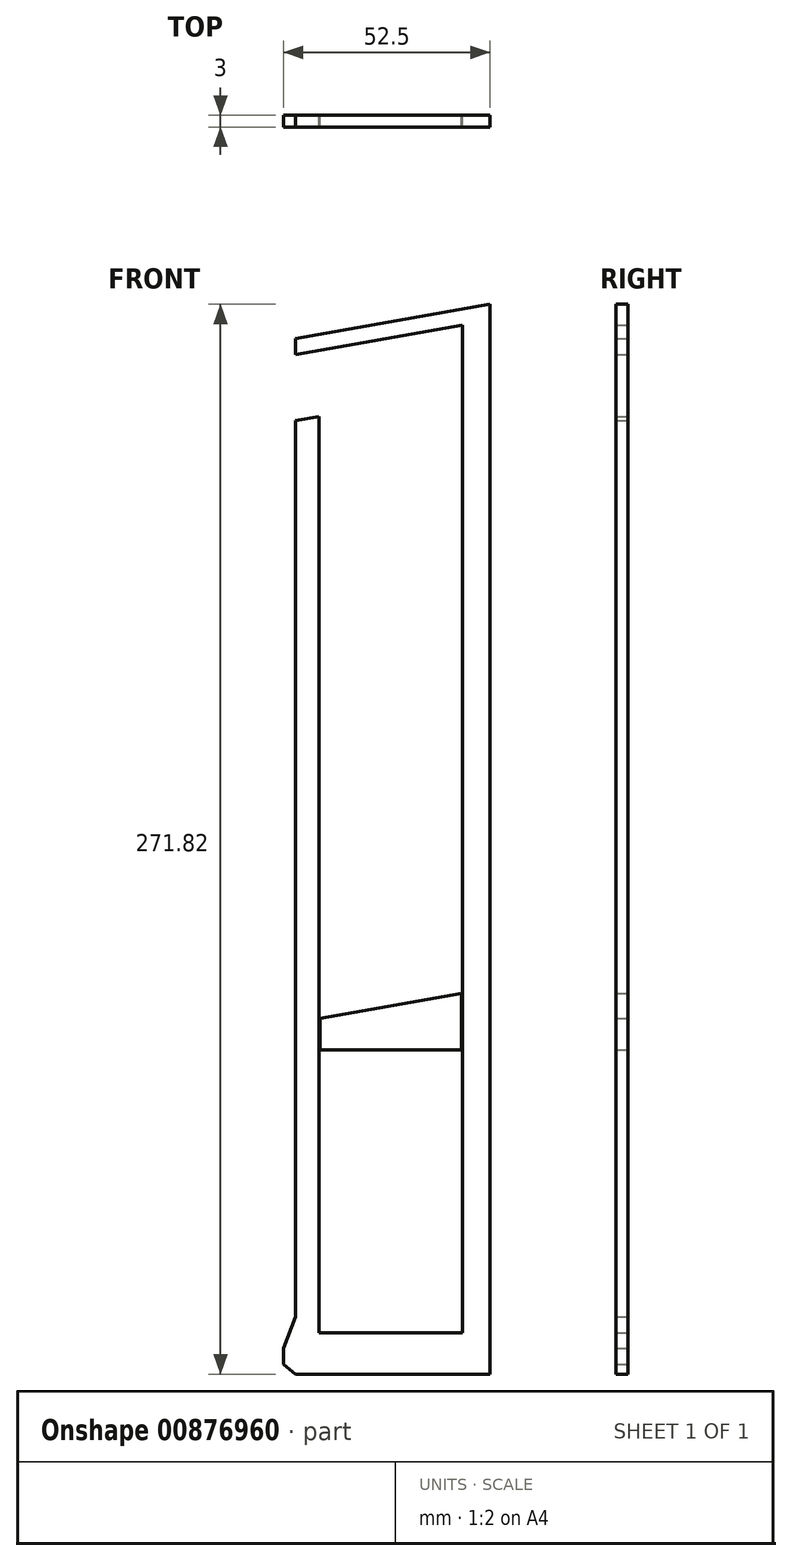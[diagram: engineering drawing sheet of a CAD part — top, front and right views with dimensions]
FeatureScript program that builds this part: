
annotation { "Feature Type Name" : "Feature", "Feature Type Description" : "" }
export const myFeature = defineFeature(function(context is Context, id is Id, definition is map)
    precondition{}
    {
        {
            var Q0;
            Q0=qCreatedBy(makeId("Front.planeOp"),FACE);
            var sketch = newSketch(context, id + "F0", { "sketchPlane" : qUnion([Q0])});
            skLineSegment(sketch, "E0", {"start": v(0, -251) * mm, "end": v(-49.5, -251) * mm});
            skPoint(sketch, "E1", {"position": v(-43.44, -7.66) * mm});
            skPoint(sketch, "E2", {"position": v(-7, -1.23) * mm});
            skLineSegment(sketch, "E3", {"start": v(-49.5, -8.73) * mm, "end": v(-43.44, -7.66) * mm});
            skLineSegment(sketch, "E4", {"start": v(-43.44, -7.66) * mm, "end": v(-43.44, -240.5) * mm});
            skLineSegment(sketch, "E5", {"start": v(-7, -1.23) * mm, "end": v(-7, -240.5) * mm});
            skLineSegment(sketch, "E6", {"start": v(-7, -240.5) * mm, "end": v(-43.44, -240.5) * mm});
            skLineSegment(sketch, "E7", {"start": v(-43.19, -168.59) * mm, "end": v(-7.25, -168.59) * mm});
            skLineSegment(sketch, "E8", {"start": v(-43.19, -168.59) * mm, "end": v(-43.19, -160.59) * mm});
            skLineSegment(sketch, "E9", {"start": v(-43.19, -160.59) * mm, "end": v(-7.25, -154.25) * mm});
            skLineSegment(sketch, "E10", {"start": v(-7.25, -154.25) * mm, "end": v(-7.25, -168.59) * mm});
            skLineSegment(sketch, "E11", {"start": v(0, 0) * mm, "end": v(0, -251) * mm});
            skLineSegment(sketch, "E12", {"start": v(-49.5, -236.5) * mm, "end": v(-52.5, -244.5) * mm});
            skLineSegment(sketch, "E13", {"start": v(-52.5, -244.5) * mm, "end": v(-52.5, -248.5) * mm});
            skLineSegment(sketch, "E14", {"start": v(-52.5, -248.5) * mm, "end": v(-49.5, -251) * mm});
            skLineSegment(sketch, "E15", {"start": v(-49.5, -236.5) * mm, "end": v(-49.5, -8.73) * mm});
            skLineSegment(sketch, "E16", {"start": v(0, 0) * mm, "end": v(0, 20.82) * mm});
            skLineSegment(sketch, "E17", {"start": v(0, 20.82) * mm, "end": v(-49.5, 12.09) * mm});
            skLineSegment(sketch, "E18", {"start": v(-7, -1.23) * mm, "end": v(-7, 15.52) * mm});
            skLineSegment(sketch, "E19", {"start": v(-7, 15.52) * mm, "end": v(-49.5, 8.03) * mm});
            skLineSegment(sketch, "E20", {"start": v(-49.5, 8.03) * mm, "end": v(-49.5, 12.09) * mm});
            skLineSegment(sketch, "E21", {"start": v(0, 0) * mm, "end": v(63.83, 0) * mm, "construction": true});
            skSolve(sketch);
        }
        {
            var Q0;
            Q0=makeQuery(id+"F0.imprint","IMPRINT",FACE,{"disambiguationData":[TD([[makeQuery(id+"F0.imprint","IMPRINT",EDGE,{"derivedFrom":sQuery(id+"F0.wireOp",EDGE,"ZOjMvmvA-9yqH-GHR5-0Tow-drmrUjQdXzBV")}),-1.0]])]});
            var Q1;
            Q1=makeQuery(id+"F0.imprint","IMPRINT",FACE,{"disambiguationData":[TD([[makeQuery(id+"F0.imprint","IMPRINT",EDGE,{"derivedFrom":sQuery(id+"F0.wireOp",EDGE,"E7")}),1.0]])]});
            extrude(context, id + "F1", {"entities" : qUnion([Q0, Q1]), "depth" : 3 * mm, "offsetDistance" : 25 * mm});
        }
        {
            var Q0;
            Q0=makeQuery(id+"F0.imprint","IMPRINT",FACE,{"disambiguationData":[TD([[makeQuery(id+"F0.imprint","IMPRINT",EDGE,{"derivedFrom":sQuery(id+"F0.wireOp",EDGE,"E0")}),-1.0]])]});
            extrude(context, id + "F2", {"entities" : qUnion([Q0]), "depth" : 3 * mm, "offsetDistance" : 25 * mm});
        }
    });
